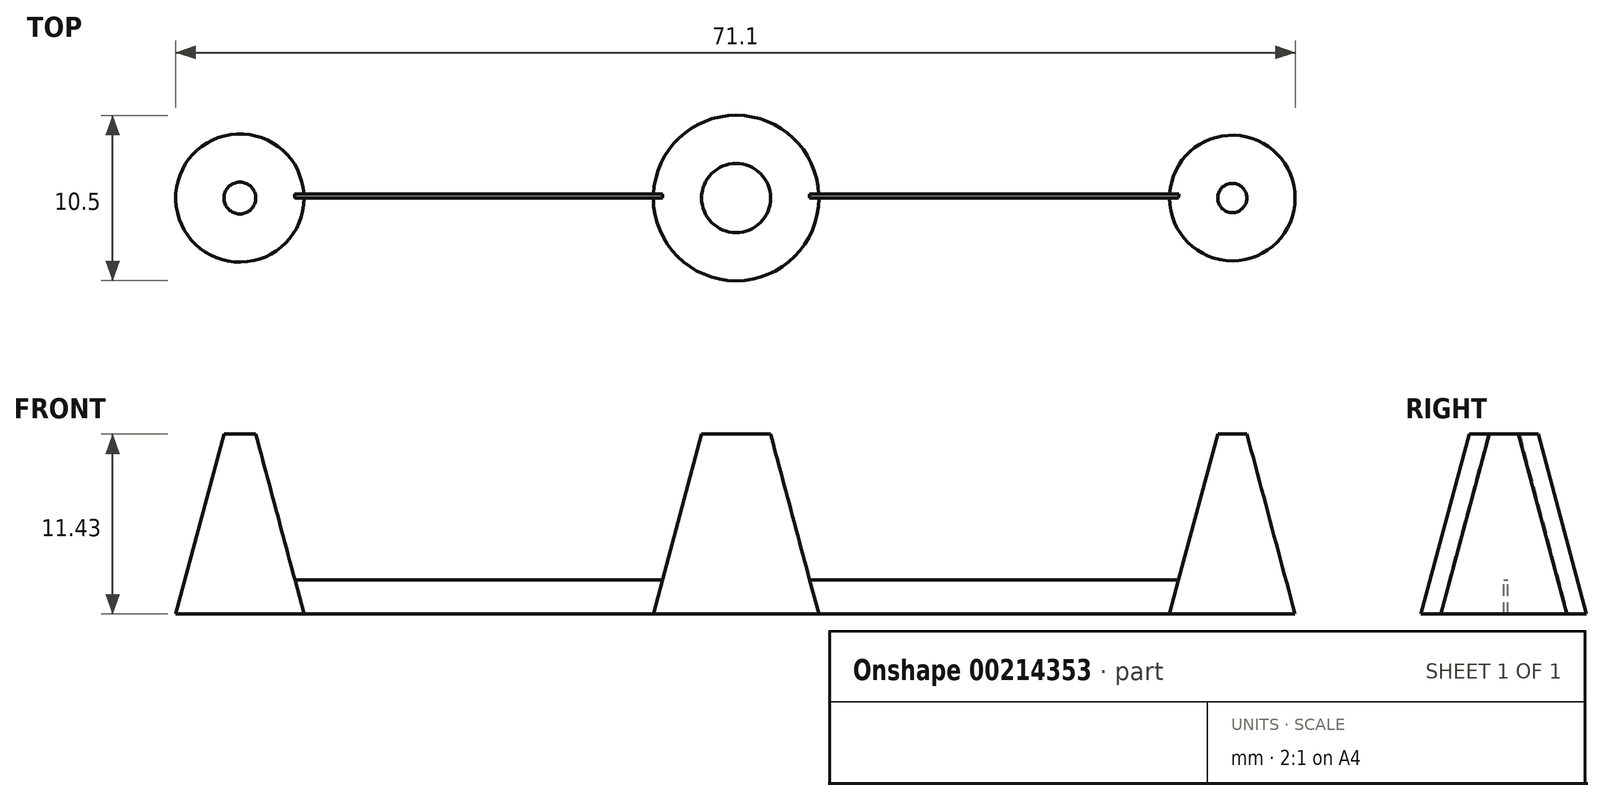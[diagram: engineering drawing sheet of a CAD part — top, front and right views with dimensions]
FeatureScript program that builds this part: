
annotation { "Feature Type Name" : "Feature", "Feature Type Description" : "" }
export const myFeature = defineFeature(function(context is Context, id is Id, definition is map)
    precondition{}
    {
        {
            var Q0;
            Q0=qCreatedBy(makeId("Top.planeOp"),FACE);
            var sketch = newSketch(context, id + "F0", { "sketchPlane" : qUnion([Q0])});
            skCircle(sketch, "E0", {"center": v(0, 0) * mm, "radius": 5.25 * mm});
            skCircle(sketch, "E1", {"center": v(-31.52, 0) * mm, "radius": 4.07 * mm});
            skCircle(sketch, "E2", {"center": v(31.52, 0) * mm, "radius": 3.99 * mm});
            skSolve(sketch);
        }
        {
            var Q0;
            Q0=makeQuery(id+"F0.imprint","IMPRINT",FACE,{"disambiguationData":[TD([[makeQuery(id+"F0.imprint","IMPRINT",EDGE,{"derivedFrom":sQuery(id+"F0.wireOp",EDGE,"E0")}),1.0]])]});
            var Q1;
            Q1=makeQuery(id+"F0.imprint","IMPRINT",FACE,{"disambiguationData":[TD([[makeQuery(id+"F0.imprint","IMPRINT",EDGE,{"derivedFrom":sQuery(id+"F0.wireOp",EDGE,"E2")}),1.0]])]});
            var Q2;
            Q2=makeQuery(id+"F0.imprint","IMPRINT",FACE,{"disambiguationData":[TD([[makeQuery(id+"F0.imprint","IMPRINT",EDGE,{"derivedFrom":sQuery(id+"F0.wireOp",EDGE,"E1")}),1.0]])]});
            extrude(context, id + "F1", {"entities" : qUnion([Q0, Q1, Q2]), "depth" : 11.43 * mm, "hasDraft" : true, "draftAngle" : 15 * degree, "draftPullDirection" : true});
        }
        {
            var Q0;
            Q0=qCreatedBy(makeId("Front.planeOp"),FACE);
            var sketch = newSketch(context, id + "F2", { "sketchPlane" : qUnion([Q0])});
            skLineSegment(sketch, "E3", {"start": v(-31.09, 0) * mm, "end": v(0, 0) * mm});
            skLineSegment(sketch, "E4", {"start": v(0, 0) * mm, "end": v(32.42, 0) * mm});
            skLineSegment(sketch, "E5", {"start": v(32.42, 0) * mm, "end": v(32.42, 2.16) * mm});
            skLineSegment(sketch, "E6", {"start": v(32.42, 2.16) * mm, "end": v(0, 2.16) * mm});
            skLineSegment(sketch, "E7", {"start": v(0, 2.16) * mm, "end": v(-31.54, 2.16) * mm});
            skLineSegment(sketch, "E8", {"start": v(-31.54, 2.16) * mm, "end": v(-31.09, 0) * mm});
            skSolve(sketch);
        }
        {
            var Q0;
            Q0 = qSketchRegion(id + "F2", true);
            extrude(context, id + "F3", {"entities" : qUnion([Q0]), "operationType" : NewBodyOperationType.ADD, "oppositeDirection" : true, "depth" : 0.25 * mm});
        }
    });
